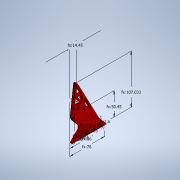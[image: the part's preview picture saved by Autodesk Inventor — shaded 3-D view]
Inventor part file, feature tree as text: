
AUTODESK INVENTOR PART (.ipt)
format: ipt  version: 2020 (Build 240168000, 168)  size: 527,872 bytes
history: native  units: mm
features: extrude x3, fillet x3, sketch x3, projected_geometry x1
ambient origin geometry x8: Origin, YZ Plane, XZ Plane, XY Plane, X Axis, Y Axis, Z Axis, Center Point
bodies: Solid1 (feature_tree)
feature tree (10):
  extrude  "Extrusion1"  Depth=27.0mm
  extrude  "Extrusion9"  Depth=27.8mm
  fillet  "Fillet2"  Radius=50.45mm
  fillet  "Fillet3"  Radius=10.0mm
  extrude  "Extrusion8"  Depth=6.8mm
  fillet  "Fillet4"  Radius=1.6mm
  sketch  "Sketch1"  dims[d0=45.0deg d1=27.0mm]
  sketch  "Sketch8"  dims[d5=5.0mm d6=0.0mm d34=27.8mm d40=50.45mm d47=10.0mm]
  projected_geometry  "Projected Loop6"
  sketch  "Sketch9"  dims[d55=4.8mm d56=6.8mm d57=1.6mm d58=30.0mm d60=16.333333mm d61=10.0mm d63=10.0mm d65=5.0mm d66=10.0mm d67=107.032605mm d71=3.0mm d72=3.0mm d75=0.5mm d76=3.6mm d77=12.0mm d78=20.0mm d79=0.0mm d80=0.0mm d81=49.0mm d88=1.0mm d94=1.5mm d95=1.5mm d96=1.5mm d97=1.5mm d98=3.0mm d99=0.0mm d100=14.45mm d102=76.0mm d103=3.1mm d104=10.0mm d105=30.0mm d106=3.1mm d108=56.0mm d109=10.0mm d110=6.108652mm d50=0.5mm d51=0.872665mm d52=0.5mm d53=0.872665mm d111=0.872665mm d112=0.5mm d113=0.872665mm]
